# Revit family: Bisley_Essentials_Tambour_1000mm_Wide
name_source: partatom
category: Furniture
revit_build: Autodesk Revit 2018 (Build: 20170223_1515(x64)
units: mm (PartAtom-declared; Revit-internal decimal feet)

## family parameters
Always vertical = No
Cut with Voids When Loaded = No
OmniClass Number = 23.40.20.00
OmniClass Title = General Furniture and Specialties
Room Calculation Point = No
Shared = No
Work Plane-Based = No

## types (14) — shared parameters
Bisely_Width = 1000 mm  [stored 3.28084 ft]
Bisley_Depth = 470 mm
Category = Furniture
Manufacturer = Bisley
URL = www.bisley.com
Uniclass2015Code = Pr_40_30_78
Uniclass2015Title = Shelves and storage units
Uniclass2015Version = v1.5
WarrantyDurationUnit = 5 Years

## per-type parameters (varying)
| type | Bisley_Height | Bisley_Tambour_Material | Description | ManufacturerName | Plinth | Type Comments |
| YETB1007/1S | 693 mm | <By Category> | Essentials 1000mm wide Tambour including 1 shelf |  | 43 mm | Height is adjustable up to 8mm (0.3”) in total |
| YETBDH1007/1S | 718 mm | <By Category> | Essentials Desk High 1000mm wide Tambour including 1 shelf | Bisley | 43 mm | Height is adjustable up to 8mm (0.3”) in total |
| YETB1010 | 1000 mm  [stored 3.28084 ft] | <By Category> | Essentials 1000mm wide Tambour, empty | Bisley | 87 mm | Height is adjustable up to 24mm (1”) in total |
| YETB1010/1S | 1000 mm  [stored 3.28084 ft] | <By Category> | Essentials 1000mm wide Tambour including 1 shelf | Bisley | 87 mm | Height is adjustable up to 24mm (1”) in total |
| YETB1011 | 1070 mm | <By Category> | Essentials 1000mm wide Tambour, empty | Bisley | 87 mm | Height is adjustable up to 24mm (1”) in total |
| YETB1011/1S | 1070 mm | <By Category> | Essentials 1000mm wide Tambour including 1 shelf | Bisley | 87 mm | Height is adjustable up to 24mm (1”) in total |
| YETB1012 | 1270 mm | <By Category> | Essentials 1000mm wide Tambour, empty | Bisley | 87 mm | Height is adjustable up to 24mm (1”) in total |
| YETB1012/2S | 1270 mm | <By Category> | Essentials 1000mm wide Tambour including 2 shelves | Bisley | 87 mm | Height is adjustable up to 24mm (1”) in total |
| YETB1015 | 1570 mm | <By Category> | Essentials 1000mm wide Tambour, empty | Bisley | 87 mm | Height is adjustable up to 24mm (1”) in total |
| YETB1015/3S | 1570 mm | <By Category> | Essentials 1000mm wide Tambour including 3 shelves | Bisley | 87 mm | Height is adjustable up to 24mm (1”) in total |
| YETB1019 | 1970 mm | <By Category> | Essentials 1000mm wide Tambour, empty | Bisley | 87 mm | Height is adjustable up to 24mm (1”) in total |
| YETB1019/4S | 1970 mm | <By Category> | Essentials 1000mm wide Tambour including 4 shelves | Bisley | 87 mm | Height is adjustable up to 24mm (1”) in total |
| YETB1022 | 2270 mm | Bisley - ARN - Silver | Essentials 1000mm wide Tambour, empty | Bisley | 87 mm | Height is adjustable up to 24mm (1”) in total |
| YETB1022/5S | 2270 mm | <By Category> | Essentials 1000mm wide Tambour including 5 shelves | Bisley | 87 mm | Height is adjustable up to 24mm (1”) in total |

note: column(s) folded — value = type name in every type: Model

note: [stored X ft] marks values corroborated as IEEE doubles in the binary element streams (Revit-internal decimal feet)

## geometry (parser evidence)
native form markers: Sweep x9
no freeform markers — native parametric forms only
